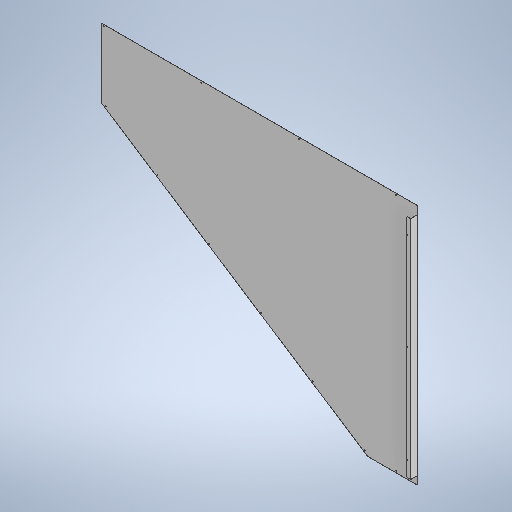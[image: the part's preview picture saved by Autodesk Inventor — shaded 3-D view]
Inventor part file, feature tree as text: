
AUTODESK INVENTOR PART (.ipt)
format: ipt  version: 2025 (Build 290162010, 162A)  size: 429,568 bytes
history: native  units: mm
features: sheet_metal_op x7, sketch x6, extrude x4, other x4, projected_geometry x4, pattern_linear x3, chamfer x1
ambient origin geometry x8: Origin, YZ Plane, XZ Plane, XY Plane, X Axis, Y Axis, Z Axis, Center Point
bodies: Solid1 (feature_tree)
feature tree (29):
  sheet_metal_op  "Face1"
  sheet_metal_op  "Flange1"
  sheet_metal_op  "Flange2"
  extrude  "Extrusion4"  Depth=1490.0mm
  pattern_linear  "Rectangular Pattern6"  Spacing1=42.0mm  [1 undecoded]
  extrude  "Extrusion5"  Depth=10.0mm
  pattern_linear  "Rectangular Pattern7"  Spacing1=0.8mm  [1 undecoded]
  chamfer  "Corner Round1"
  extrude  "Extrusion6"  Depth=0.8mm
  extrude  "Extrusion7"  Depth=0.8mm
  pattern_linear  "Rectangular Pattern8"  Spacing1=0.4mm  [1 undecoded]
  other  "Plate1"
  sketch  "Sketch5"  dims[d0=1945.0mm d1=1490.0mm]
  other  "Plate2"
  sheet_metal_op  "Bend1"
  sheet_metal_op  "Corner1"
  sketch  "Sketch6"  dims[d2=0.8mm]
  other  "Plate3"
  sheet_metal_op  "Bend2"
  sheet_metal_op  "Corner2"
  sketch  "Sketch8"  dims[d50=0.8mm]
  projected_geometry  "Projected Loop3"
  sketch  "Sketch9"  dims[d51=0.4mm]
  projected_geometry  "Projected Loop4"
  sketch  "Sketch10"  dims[d52=1.6mm]
  projected_geometry  "Projected Loop5"
  sketch  "Sketch11"  dims[d53=0.8mm d54=42.0mm d55=90.0deg d56=0.8mm d57=3.2mm d58=0.8mm d59=0.8mm d60=0.8mm d61=0.4mm d62=1.6mm d63=0.8mm d64=25.0mm d65=90.0deg d66=0.8mm d67=3.2mm d68=0.8mm d69=0.8mm d80=50.0mm d81=50.0mm d82=5.0mm d83=18.0mm d84=0.8mm d85=0.0mm d86=30.0mm d88=600.0mm d89=10.0mm d90=6.0mm d91=15.0mm d92=0.8mm d93=0.0mm d94=40.0mm d96=600.0mm d97=6.0mm d98=425.0mm d99=305.0mm d100=0.0mm d101=0.0mm d102=10.0mm d103=30.0mm d104=0.0mm d105=0.0mm d106=60.0mm d108=380.0mm]
  projected_geometry  "Projected Loop6"
  other  "Definition1"
note: 3 required parameter values undecoded (feature->parameter linkage not recoverable at this tier; creation-order binding heuristic only, values carry confidence <= 0.55)
